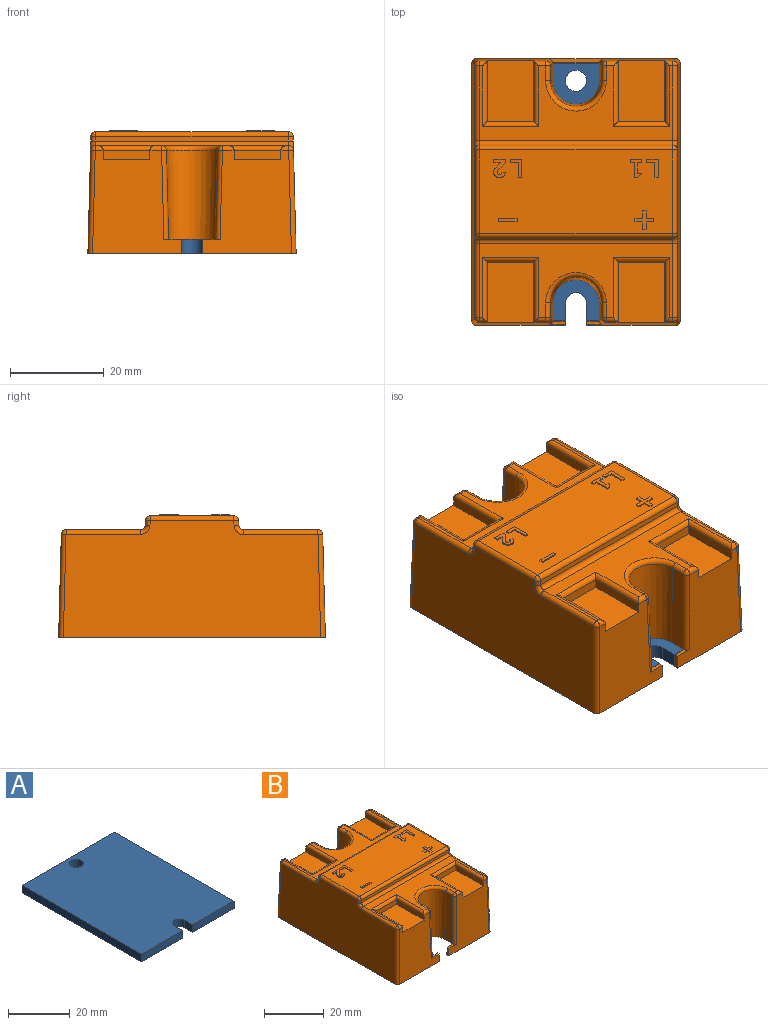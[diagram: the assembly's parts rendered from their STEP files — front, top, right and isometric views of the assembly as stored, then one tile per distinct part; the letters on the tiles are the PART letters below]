
ASSEMBLY  parts=2 mates=1
PART A: 11 faces, bbox 42.5x55x3 mm
  f0: plane 3.75x3mm, normal (1,0,0), area 11.2mm2, adj f1,f7,f9,f10
  f1: cylinder r=2.25mm len=4.5mm, axis (0,0,-1), area 21.2mm2, adj f0,f2,f9,f10
  f2: plane 3.75x3mm, normal (-1,0,0), area 11.2mm2, adj f1,f3,f9,f10
  f3: plane 19x3mm, normal (0,-1,0), area 57mm2, adj f2,f4,f9,f10
  f4: plane 55x3mm, normal (1,0,0), area 165mm2, adj f3,f5,f9,f10
  f5: plane 42.5x3mm, normal (0,1,0), area 127.5mm2, adj f4,f6,f9,f10
  f6: plane 55x3mm, normal (-1,0,0), area 165mm2, adj f5,f7,f9,f10
  f7: plane 19x3mm, normal (0,-1,0), area 57mm2, adj f0,f6,f9,f10
  f8: cylinder r=2.25mm len=4.5mm, axis (0,0,-1), area 42.4mm2, adj f9,f10
  f9: plane 55x42.5mm, normal (0,0,1), area 2296.8mm2, adj f0,f1,f2,f3,f4,f5,f6,f7
  f10: plane 55x42.5mm, normal (0,0,-1), area 2296.8mm2, adj f0,f1,f2,f3,f4,f5,f6,f7
PART B: 161 faces, bbox 44.5x57x26.3 mm
  f0: plane 41.19x17.89mm, normal (0,0,1), area 709.4mm2, adj f90,f91,f101,f102,f108,f109,f110,f111
  f1: plane 41.35x15.95mm, normal (0,0,1), area 241.7mm2, adj f45,f47,f48,f49,f51,f53,f54,f57
  f2: plane 22.03x19mm, normal (0,-1,0.03), area 315.8mm2, adj f13,f17,f18,f30,f31,f32,f64,f74
  f3: plane 42.5x22.03mm, normal (0,1,0.03), area 645.3mm2, adj f6,f18,f27,f28,f29,f38,f40,f41
  f4: plane 22.03x19mm, normal (0,-1,0.03), area 315.8mm2, adj f7,f16,f18,f34,f35,f36,f56,f66
  f5: plane 41.35x15.95mm, normal (0,0,1), area 241.7mm2, adj f55,f59,f65,f66,f70,f74,f75,f78
  f6: plane 12.02x0.86mm, normal (0,0,1), area 8.9mm2, adj f3,f10,f44,f50
  f7: plane 3.69x0.86mm, normal (0,0,1), area 2.5mm2, adj f4,f8,f16,f56
  f8: plane 19.08x3mm, normal (0,1,0.03), area 57mm2, adj f7,f9,f16,f18,f19
  f9: plane 55.16x3mm, normal (1,0,0.03), area 165.3mm2, adj f8,f10,f18,f19
  f10: plane 42.66x3mm, normal (0,-1,0.03), area 127.8mm2, adj f6,f9,f11,f18,f19
  f11: plane 55.16x3mm, normal (-1,0,0.03), area 165.3mm2, adj f10,f12,f18,f19
  f12: plane 19.08x3mm, normal (0,1,0.03), area 57mm2, adj f11,f13,f17,f18,f19
  f13: plane 3x1mm, normal (-1,0,0.03), area 2.8mm2, adj f2,f12,f17,f18
  f14: plane 55x25.03mm, normal (1,0,0.03), area 1254.7mm2, adj f18,f73,f82,f87,f92,f93,f102,f103
  f15: plane 55x25.03mm, normal (-1,0,0.03), area 1254.7mm2, adj f18,f61,f71,f76,f80,f85,f90,f95
  f16: plane 3x1mm, normal (1,0,0.03), area 2.8mm2, adj f4,f7,f8,f18
  f17: plane 3.69x0.86mm, normal (0,0,1), area 2.5mm2, adj f2,f12,f13,f64
  f18: plane 57x44.5mm, normal (0,0,-1), area 193.6mm2, adj f2,f3,f4,f8,f9,f10,f11,f12
  f19: plane 55.16x42.66mm, normal (0,0,-1), area 2197.7mm2, adj f8,f9,f10,f11,f12,f20,f21,f22
  f20: cone r=5mm half-angle=1.5deg, axis (0,0,1), area 313.9mm2, adj f19,f21,f25,f47
  f21: plane 19.03x3.67mm, normal (1,0,0.03), area 65.1mm2, adj f19,f20,f44,f45
  f22: plane 19.03x3.67mm, normal (1,0,0.03), area 65.1mm2, adj f19,f23,f55,f56
  f23: cone r=5mm half-angle=1.5deg, axis (0,0,1), area 313.9mm2, adj f19,f22,f24,f59
  f24: plane 19.03x3.67mm, normal (-1,0,0.03), area 65.1mm2, adj f19,f23,f64,f65
  f25: plane 19.03x3.67mm, normal (-1,0,0.03), area 65.1mm2, adj f19,f20,f49,f50
  f26: plane 10x2mm, normal (0,1,0), area 20mm2, adj f27,f28,f29,f53
  f27: plane 12.98x2mm, normal (-1,0,0), area 25.9mm2, adj f3,f26,f29,f51
  f28: plane 12.98x2mm, normal (1,0,0), area 25.9mm2, adj f3,f26,f29,f57
  f29: plane 12.98x10mm, normal (0,0,1), area 129.8mm2, adj f3,f26,f27,f28
  f30: plane 12.98x2mm, normal (1,0,0), area 25.9mm2, adj f2,f32,f33,f78
  f31: plane 12.98x2mm, normal (-1,0,0), area 25.9mm2, adj f2,f32,f33,f88
  f32: plane 12.98x10mm, normal (0,0,1), area 129.8mm2, adj f2,f30,f31,f33
  f33: plane 10x2mm, normal (0,-1,0), area 20mm2, adj f30,f31,f32,f83
  f34: plane 12.98x2mm, normal (1,0,0), area 25.9mm2, adj f4,f36,f37,f79
  f35: plane 12.98x2mm, normal (-1,0,0), area 25.9mm2, adj f4,f36,f37,f70
  f36: plane 12.98x10mm, normal (0,0,1), area 129.8mm2, adj f4,f34,f35,f37
  f37: plane 10x2mm, normal (0,-1,0), area 20mm2, adj f34,f35,f36,f75
  f38: plane 12.98x2mm, normal (1,0,0), area 25.9mm2, adj f3,f39,f41,f58
  f39: plane 10x2mm, normal (0,1,0), area 20mm2, adj f38,f40,f41,f63
  f40: plane 12.98x2mm, normal (-1,0,0), area 25.9mm2, adj f3,f39,f41,f68
  f41: plane 12.98x10mm, normal (0,0,1), area 129.8mm2, adj f3,f38,f39,f40
  f42: plane 41.25x1.05mm, normal (0,1,0.03), area 43.4mm2, adj f80,f81,f91,f92
  f43: plane 41.25x1.05mm, normal (0,-1,0.03), area 43.4mm2, adj f96,f101,f104,f107
  f44: cylinder r=1mm len=19.04mm, axis (0.03,0.03,-1), area 29.9mm2, adj f3,f6,f19,f21,f46
  f45: cylinder r=1mm len=3.17mm, axis (0,1,0), area 4.9mm2, adj f1,f21,f46,f47
  f46: sphere r=1mm, area 1.5mm2, adj f44,f45,f48
  f47: torus R=6.5mm, axis (0,0,1), area 28.5mm2, adj f1,f20,f45,f49
  f48: cylinder r=1mm len=2.5mm, axis (1,0,0), area 3.3mm2, adj f1,f3,f46,f51
  f49: cylinder r=1mm len=3.17mm, axis (0,-1,0), area 4.9mm2, adj f1,f25,f47,f52
  f50: cylinder r=1mm len=19.04mm, axis (-0.03,0.03,-1), area 29.9mm2, adj f3,f6,f19,f25,f52
  f51: cylinder r=1mm len=13.92mm, axis (0,-1,0), area 20.3mm2, adj f1,f3,f27,f48,f53
  f52: sphere r=1mm, area 1.5mm2, adj f49,f50,f54
  f53: cylinder r=1mm len=12mm, axis (-1,0,0), area 16.8mm2, adj f1,f26,f51,f57
  f54: cylinder r=1mm len=2.5mm, axis (1,0,0), area 3.3mm2, adj f1,f3,f52,f58
  f55: cylinder r=1mm len=3.17mm, axis (0,-1,0), area 4.9mm2, adj f5,f22,f59,f60
  f56: cylinder r=1mm len=19.04mm, axis (0.03,-0.03,-1), area 29.9mm2, adj f4,f7,f19,f22,f60
  f57: cylinder r=1mm len=13.92mm, axis (0,1,0), area 20.3mm2, adj f1,f3,f28,f53,f62
  f58: cylinder r=1mm len=13.92mm, axis (0,1,0), area 20.3mm2, adj f1,f3,f38,f54,f63
  f59: torus R=6.5mm, axis (0,0,1), area 28.5mm2, adj f5,f23,f55,f65
  f60: sphere r=1mm, area 1.5mm2, adj f55,f56,f66
  f61: cylinder r=1mm len=22.05mm, axis (-0.03,0.03,-1), area 34.6mm2, adj f3,f15,f18,f67
  f62: cylinder r=1mm len=1.67mm, axis (1,0,0), area 2mm2, adj f1,f3,f57,f67
  f63: cylinder r=1mm len=12mm, axis (-1,0,0), area 16.8mm2, adj f1,f39,f58,f68
  f64: cylinder r=1mm len=19.04mm, axis (-0.03,-0.03,-1), area 29.9mm2, adj f2,f17,f19,f24,f69
  f65: cylinder r=1mm len=3.17mm, axis (0,-1,0), area 4.9mm2, adj f5,f24,f59,f69
  f66: cylinder r=1mm len=2.5mm, axis (1,0,0), area 3.3mm2, adj f4,f5,f60,f70
  f67: sphere r=1mm, area 1.5mm2, adj f61,f62,f71
  f68: cylinder r=1mm len=13.92mm, axis (0,-1,0), area 20.3mm2, adj f1,f3,f40,f63,f72
  f69: sphere r=1mm, area 1.5mm2, adj f64,f65,f74
  f70: cylinder r=1mm len=13.92mm, axis (0,-1,0), area 20.3mm2, adj f4,f5,f35,f66,f75
  f71: cylinder r=1mm len=15.95mm, axis (0,-1,0), area 24.6mm2, adj f1,f15,f67,f76
  f72: cylinder r=1mm len=1.67mm, axis (1,0,0), area 2mm2, adj f1,f3,f68,f77
  f73: cylinder r=1mm len=22.05mm, axis (0.03,0.03,-1), area 34.6mm2, adj f3,f14,f18,f77
  f74: cylinder r=1mm len=2.5mm, axis (1,0,0), area 3.3mm2, adj f2,f5,f69,f78
  f75: cylinder r=1mm len=12mm, axis (1,0,0), area 16.8mm2, adj f5,f37,f70,f79
  f76: bspline ~2x1.96mm, area 3.3mm2, adj f15,f71,f80,f81
  f77: sphere r=1mm, area 1.5mm2, adj f72,f73,f82
  f78: cylinder r=1mm len=13.92mm, axis (0,1,0), area 20.3mm2, adj f2,f5,f30,f74,f83
  f79: cylinder r=1mm len=13.92mm, axis (0,1,0), area 20.3mm2, adj f4,f5,f34,f75,f84
  f80: cylinder r=1mm len=1.06mm, axis (-0.03,0.03,-1), area 1.7mm2, adj f15,f42,f76,f86
  f81: cylinder r=1mm len=41.35mm, axis (-1,0,0), area 63.8mm2, adj f1,f42,f76,f87
  f82: cylinder r=1mm len=15.95mm, axis (0,-1,0), area 24.6mm2, adj f1,f14,f77,f87
  f83: cylinder r=1mm len=12mm, axis (1,0,0), area 16.8mm2, adj f5,f33,f78,f88
  f84: cylinder r=1mm len=1.67mm, axis (1,0,0), area 2mm2, adj f4,f5,f79,f89
  f85: cylinder r=1mm len=22.05mm, axis (-0.03,-0.03,-1), area 34.6mm2, adj f4,f15,f18,f89
  f86: sphere r=1mm, area 1.5mm2, adj f80,f90,f91
  f87: bspline ~2x1.96mm, area 3.3mm2, adj f14,f81,f82,f92
  f88: cylinder r=1mm len=13.92mm, axis (0,-1,0), area 20.3mm2, adj f2,f5,f31,f83,f94
  f89: sphere r=1mm, area 1.5mm2, adj f84,f85,f95
  f90: cylinder r=1mm len=17.89mm, axis (0,-1,0), area 27.6mm2, adj f0,f15,f86,f97
  f91: cylinder r=1mm len=41.19mm, axis (1,0,0), area 63.6mm2, adj f0,f42,f86,f98
  f92: cylinder r=1mm len=1.06mm, axis (0.03,0.03,-1), area 1.7mm2, adj f14,f42,f87,f98
  f93: cylinder r=1mm len=22.05mm, axis (0.03,-0.03,-1), area 34.6mm2, adj f2,f14,f18,f99
  f94: cylinder r=1mm len=1.67mm, axis (1,0,0), area 2mm2, adj f2,f5,f88,f99
  f95: cylinder r=1mm len=15.95mm, axis (0,-1,0), area 24.6mm2, adj f5,f15,f89,f100
  f96: cylinder r=1mm len=1.06mm, axis (-0.03,-0.03,-1), area 1.7mm2, adj f15,f43,f97,f100
  f97: sphere r=1mm, area 1.5mm2, adj f90,f96,f101
  f98: sphere r=1mm, area 1.5mm2, adj f91,f92,f102
  f99: sphere r=1mm, area 1.5mm2, adj f93,f94,f103
  f100: bspline ~2x1.96mm, area 3.3mm2, adj f15,f95,f96,f104
  f101: cylinder r=1mm len=41.19mm, axis (1,0,0), area 63.6mm2, adj f0,f43,f97,f105
  f102: cylinder r=1mm len=17.89mm, axis (0,-1,0), area 27.6mm2, adj f0,f14,f98,f105
  f103: cylinder r=1mm len=15.95mm, axis (0,-1,0), area 24.6mm2, adj f5,f14,f99,f106
  f104: cylinder r=1mm len=41.35mm, axis (-1,0,0), area 63.8mm2, adj f5,f43,f100,f106
  f105: sphere r=1mm, area 1.5mm2, adj f101,f102,f107
  f106: bspline ~2x1.96mm, area 3.3mm2, adj f14,f103,f104,f107
  f107: cylinder r=1mm len=1.06mm, axis (0.03,-0.03,-1), area 1.7mm2, adj f14,f43,f105,f106
  f108: plane 4x0.25mm, normal (0,1,0), area 1mm2, adj f0,f109,f111,f112
  f109: plane 0.75x0.25mm, normal (-1,0,0), area 0.2mm2, adj f0,f108,f110,f112
  f110: plane 4x0.25mm, normal (0,-1,0), area 1mm2, adj f0,f109,f111,f112
  f111: plane 0.75x0.25mm, normal (1,0,0), area 0.2mm2, adj f0,f108,f110,f112
  f112: plane 4x0.75mm, normal (0,0,1), area 3mm2, adj f108,f109,f110,f111
  f113: plane 1.63x0.25mm, normal (0,1,0), area 0.4mm2, adj f0,f114,f124,f125
  f114: plane 0.75x0.25mm, normal (-1,0,0), area 0.2mm2, adj f0,f113,f115,f125
  f115: plane 1.63x0.25mm, normal (0,-1,0), area 0.4mm2, adj f0,f114,f116,f125
  f116: plane 1.63x0.25mm, normal (-1,0,0), area 0.4mm2, adj f0,f115,f117,f125
  f117: plane 0.75x0.25mm, normal (0,-1,0), area 0.2mm2, adj f0,f116,f118,f125
  f118: plane 1.63x0.25mm, normal (1,0,0), area 0.4mm2, adj f0,f117,f119,f125
  f119: plane 1.63x0.25mm, normal (0,-1,0), area 0.4mm2, adj f0,f118,f120,f125
  f120: plane 0.75x0.25mm, normal (1,0,0), area 0.2mm2, adj f0,f119,f121,f125
  f121: plane 1.63x0.25mm, normal (0,1,0), area 0.4mm2, adj f0,f120,f122,f125
  f122: plane 1.63x0.25mm, normal (1,0,0), area 0.4mm2, adj f0,f121,f123,f125
  f123: plane 0.75x0.25mm, normal (0,1,0), area 0.2mm2, adj f0,f122,f124,f125
  f124: plane 1.63x0.25mm, normal (-1,0,0), area 0.4mm2, adj f0,f113,f123,f125
  f125: plane 4x4mm, normal (0,0,1), area 5.4mm2, adj f113,f114,f115,f116,f117,f118,f119,f120
  f126: plane 4x0.25mm, normal (1,0,0), area 1mm2, adj f0,f127,f131,f132
  f127: plane 2.5x0.25mm, normal (0,1,0), area 0.6mm2, adj f0,f126,f128,f132
  f128: plane 0.75x0.25mm, normal (-1,0,0), area 0.2mm2, adj f0,f127,f129,f132
  f129: plane 1.75x0.25mm, normal (0,-1,0), area 0.4mm2, adj f0,f128,f130,f132
  f130: plane 3.25x0.25mm, normal (-1,0,0), area 0.8mm2, adj f0,f129,f131,f132
  f131: plane 0.75x0.25mm, normal (0,-1,0), area 0.2mm2, adj f0,f126,f130,f132
  f132: plane 4x2.5mm, normal (0,0,1), area 4.3mm2, adj f126,f127,f128,f129,f130,f131
  f133: plane 0.75x0.25mm, normal (1,0,0), area 0.2mm2, adj f0,f134,f142,f143
  f134: plane 2.5x0.25mm, normal (0,1,0), area 0.6mm2, adj f0,f133,f135,f143
  f135: plane 0.75x0.25mm, normal (-1,0,0), area 0.2mm2, adj f0,f134,f136,f143
  f136: plane 0.88x0.25mm, normal (0,-1,0), area 0.2mm2, adj f0,f135,f137,f143
  f137: plane 3.25x0.25mm, normal (-1,0,0), area 0.8mm2, adj f0,f136,f138,f143
  f138: plane 0.75x0.25mm, normal (0,-1,0), area 0.2mm2, adj f0,f137,f139,f143
  f139: plane 1x0.88mm, normal (0.75,-0.66,0), area 0.3mm2, adj f0,f138,f140,f143
  f140: plane 0.88x0.25mm, normal (0,1,0), area 0.2mm2, adj f0,f139,f141,f143
  f141: plane 2.25x0.25mm, normal (1,0,0), area 0.6mm2, adj f0,f140,f142,f143
  f142: plane 0.88x0.25mm, normal (0,-1,0), area 0.2mm2, adj f0,f133,f141,f143
  f143: plane 4x2.5mm, normal (0,0,1), area 4.8mm2, adj f133,f134,f135,f136,f137,f138,f139,f140
  f144: plane 4x0.25mm, normal (1,0,0), area 1mm2, adj f0,f145,f149,f150
  f145: plane 2.5x0.25mm, normal (0,1,0), area 0.6mm2, adj f0,f144,f146,f150
  f146: plane 0.75x0.25mm, normal (-1,0,0), area 0.2mm2, adj f0,f145,f147,f150
  f147: plane 1.75x0.25mm, normal (0,-1,0), area 0.4mm2, adj f0,f146,f148,f150
  f148: plane 3.25x0.25mm, normal (-1,0,0), area 0.8mm2, adj f0,f147,f149,f150
  f149: plane 0.75x0.25mm, normal (0,-1,0), area 0.2mm2, adj f0,f144,f148,f150
  f150: plane 4x2.5mm, normal (0,0,1), area 4.3mm2, adj f144,f145,f146,f147,f148,f149
  f151: plane 1.65x1.61mm, normal (0.72,-0.7,0), area 0.6mm2, adj f0,f152,f159,f160
  f152: plane 0.75x0.25mm, normal (1,0,0), area 0.2mm2, adj f0,f151,f153,f160
  f153: plane 2.5x0.25mm, normal (0,1,0), area 0.6mm2, adj f0,f152,f154,f160
  f154: plane 0.75x0.25mm, normal (-1,0,0), area 0.2mm2, adj f0,f153,f155,f160
  f155: plane 1.45x0.25mm, normal (0,-1,0), area 0.4mm2, adj f0,f154,f156,f160
  f156: plane 1.13x1.1mm, normal (-0.72,0.7,0), area 0.4mm2, adj f0,f155,f157,f160
  f157: cylinder r=1.25mm len=2.5mm, axis (0,0,-1), area 1.2mm2, adj f0,f156,f158,f160
  f158: plane 0.75x0.25mm, normal (0,1,0), area 0.2mm2, adj f0,f157,f159,f160
  f159: cylinder r=0.5mm len=1mm, axis (0,0,-1), area 0.5mm2, adj f0,f151,f158,f160
  f160: plane 4x2.5mm, normal (0,0,1), area 5.9mm2, adj f151,f152,f153,f154,f155,f156,f157,f158
PLACE A at identity fixed
PLACE B at identity
MATE fastened A.f8 <-> B.f20  axis (0,0,1) through (0,23.75,3)mm
